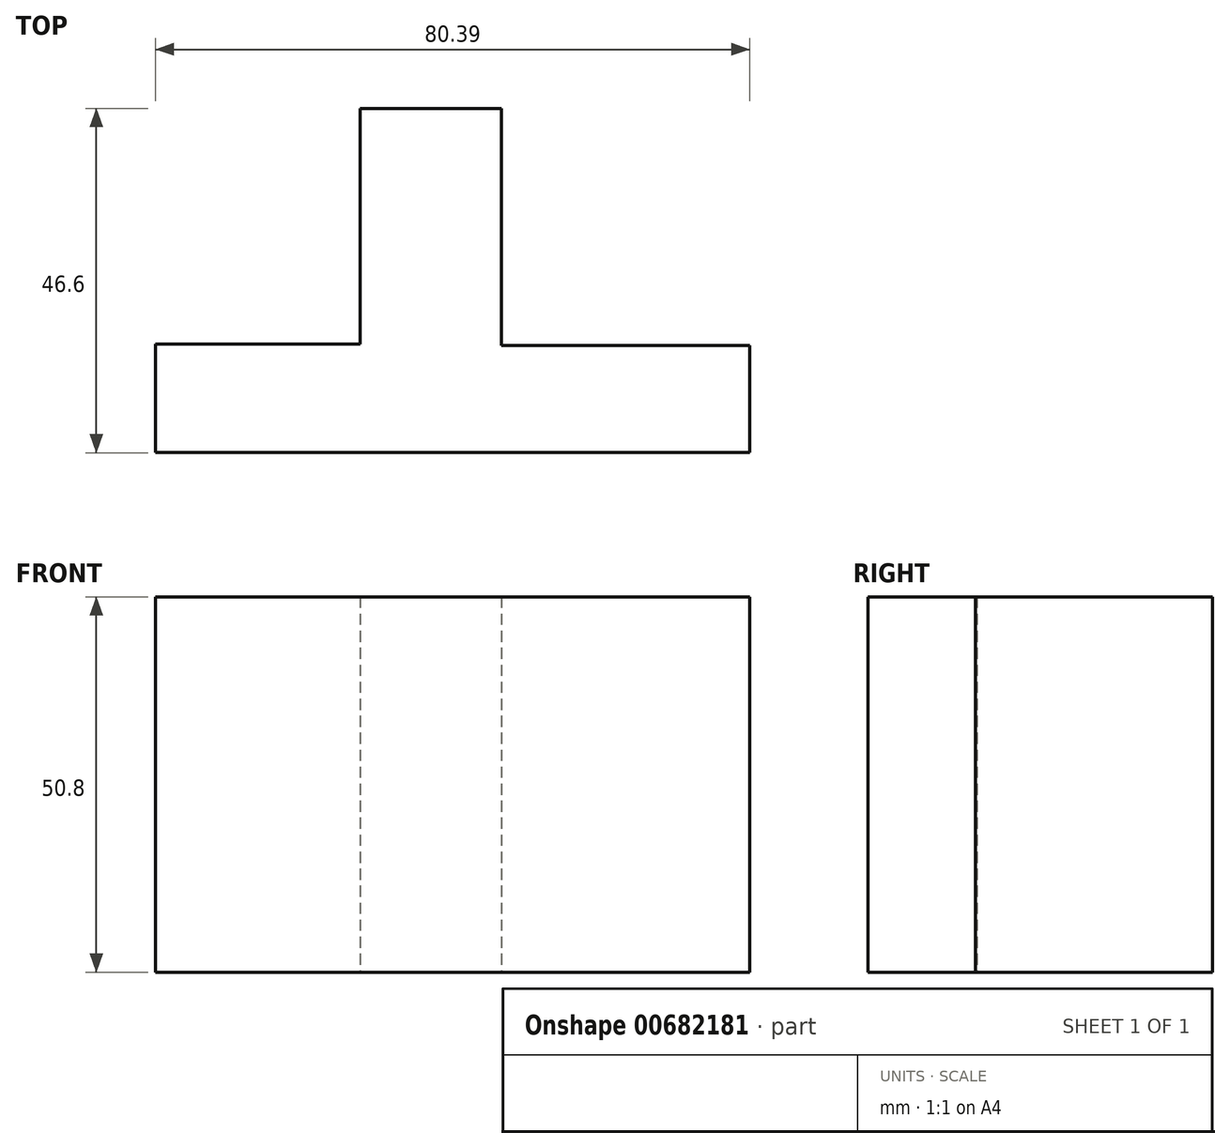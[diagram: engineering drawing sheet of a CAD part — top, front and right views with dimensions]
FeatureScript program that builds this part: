
annotation { "Feature Type Name" : "Feature", "Feature Type Description" : "" }
export const myFeature = defineFeature(function(context is Context, id is Id, definition is map)
    precondition{}
    {
        {
            var Q0;
            Q0=qCreatedBy(makeId("Top.planeOp"),FACE);
            var sketch = newSketch(context, id + "F0", { "sketchPlane" : qUnion([Q0])});
            skLineSegment(sketch, "E0", {"start": v(-23.58, -9.83) * mm, "end": v(-51.27, -9.83) * mm});
            skLineSegment(sketch, "E1", {"start": v(-51.27, -9.83) * mm, "end": v(-51.27, -24.54) * mm});
            skLineSegment(sketch, "E2", {"start": v(-51.27, -24.54) * mm, "end": v(29.12, -24.54) * mm});
            skLineSegment(sketch, "E3", {"start": v(29.12, -24.54) * mm, "end": v(29.12, -10.03) * mm});
            skLineSegment(sketch, "E4", {"start": v(29.12, -10.03) * mm, "end": v(-4.49, -10.03) * mm});
            skLineSegment(sketch, "E5", {"start": v(-4.49, -10.03) * mm, "end": v(-4.49, 22.06) * mm});
            skLineSegment(sketch, "E6", {"start": v(-4.49, 22.06) * mm, "end": v(-23.58, 22.06) * mm});
            skLineSegment(sketch, "E7", {"start": v(-23.58, 22.06) * mm, "end": v(-23.58, -11.55) * mm});
            skLineSegment(sketch, "E8", {"start": v(-23.58, -11.55) * mm, "end": v(-23.58, -9.83) * mm});
            skSolve(sketch);
        }
        {
            var Q0;
            Q0 = qSketchRegion(id + "F0", true);
            extrude(context, id + "F1", {"entities" : qUnion([Q0]), "depth" : 50.8 * mm, "offsetDistance" : 25.4 * mm});
        }
    });
